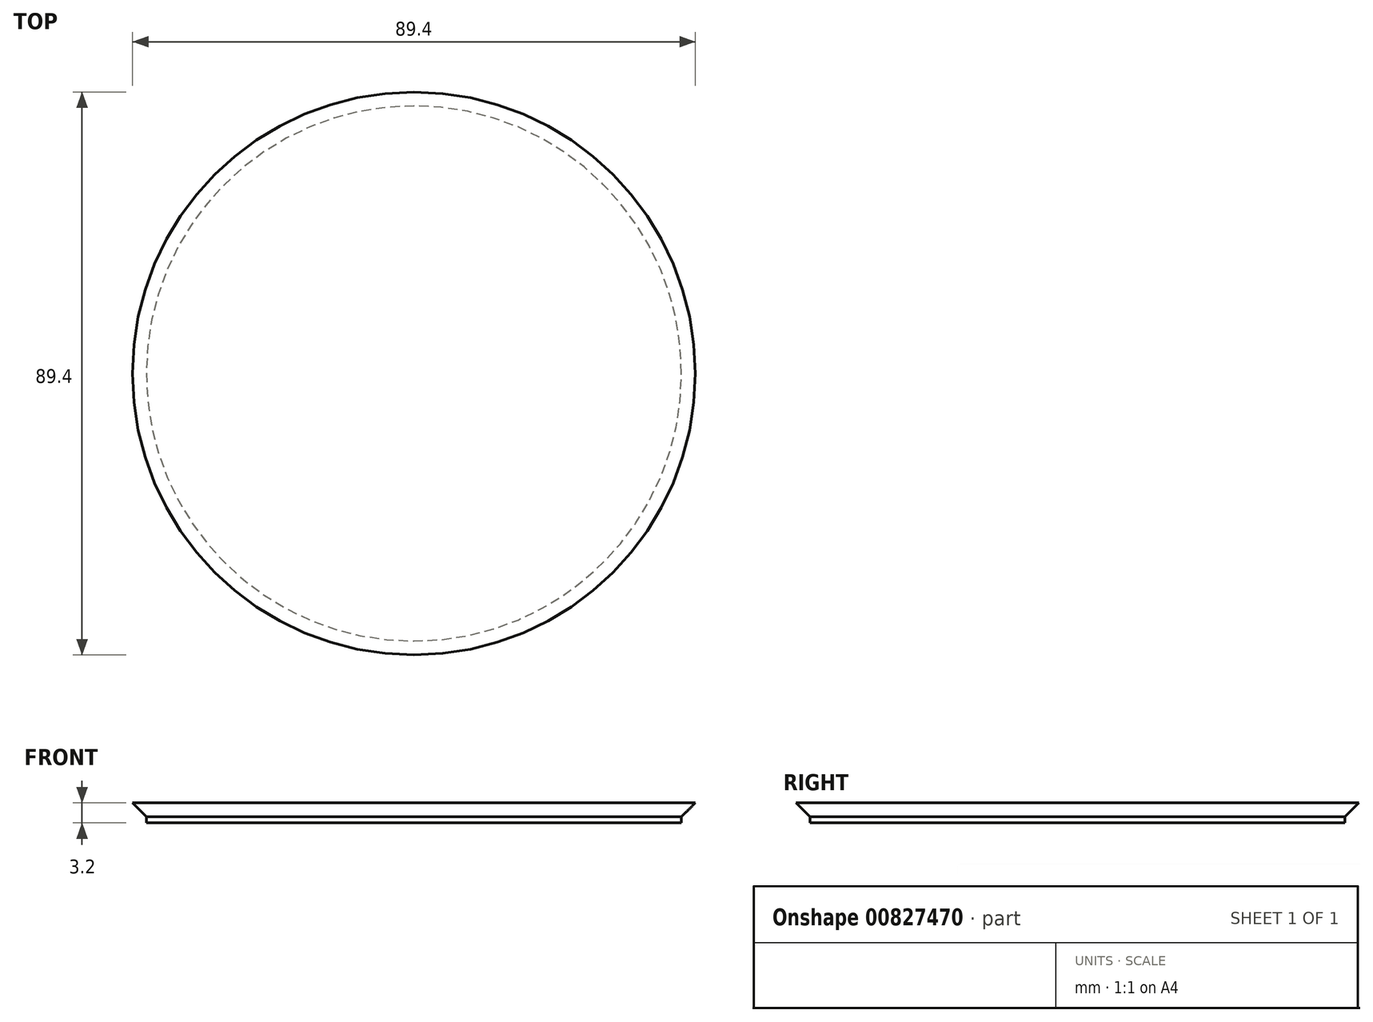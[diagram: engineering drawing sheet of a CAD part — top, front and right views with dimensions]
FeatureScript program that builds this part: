
annotation { "Feature Type Name" : "Feature", "Feature Type Description" : "" }
export const myFeature = defineFeature(function(context is Context, id is Id, definition is map)
    precondition{}
    {
        {
            var Q0;
            Q0=qCreatedBy(makeId("Top.planeOp"),FACE);
            var sketch = newSketch(context, id + "F0", { "sketchPlane" : qUnion([Q0])});
            skCircle(sketch, "E0", {"center": v(0, 0) * mm, "radius": 42.5 * mm});
            skSolve(sketch);
        }
        {
            var Q0;
            Q0=makeQuery(id+"F0.imprint","IMPRINT",FACE,{"disambiguationData":[TD([[makeQuery(id+"F0.imprint","IMPRINT",EDGE,{"derivedFrom":sQuery(id+"F0.wireOp",EDGE,"E0")}),1.0]])]});
            extrude(context, id + "F1", {"entities" : qUnion([Q0]), "depth" : 1 * mm, "offsetDistance" : 25 * mm});
        }
        {
            var Q0;
            Q0=makeQuery(id+"F1.opExtrude","CAP_FACE",FACE,{"disambiguationData":[OSD([sQuery(id+"F0.wireOp",EDGE,"E0")])],"isStart":false});
            extrude(context, id + "F2", {"entities" : qUnion([Q0]), "operationType" : NewBodyOperationType.ADD, "depth" : 2.2 * mm, "offsetDistance" : 25 * mm, "hasDraft" : true, "draftAngle" : 45 * degree});
        }
    });
